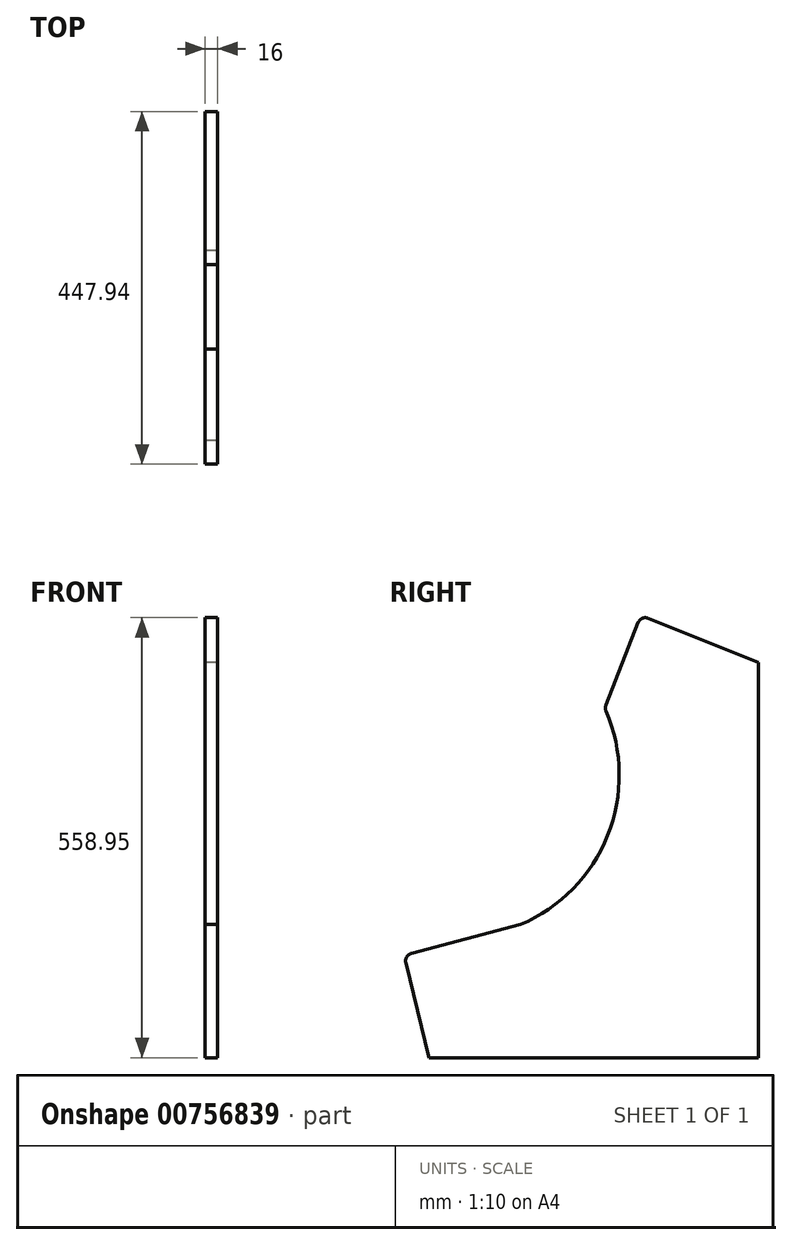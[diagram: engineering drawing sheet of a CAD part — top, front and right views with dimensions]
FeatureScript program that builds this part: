
annotation { "Feature Type Name" : "Feature", "Feature Type Description" : "" }
export const myFeature = defineFeature(function(context is Context, id is Id, definition is map)
    precondition{}
    {
        {
            var Q0;
            Q0=qCreatedBy(makeId("Right.planeOp"),FACE);
            var sketch = newSketch(context, id + "F0", { "sketchPlane" : qUnion([Q0])});
            skLineSegment(sketch, "E0.bottom", {"start": v(209, -251) * mm, "end": v(-209, -251) * mm});
            skLineSegment(sketch, "E0.left", {"start": v(209, -251) * mm, "end": v(209, 251) * mm});
            skPoint(sketch, "E0.middle", {"position": v(0, 0) * mm});
            skLineSegment(sketch, "E1", {"start": v(56.33, 301.57) * mm, "end": v(15.56, 196.86) * mm});
            skLineSegment(sketch, "E2", {"start": v(-93, -82) * mm, "end": v(-231.49, -118.5) * mm});
            skLineSegment(sketch, "E3", {"start": v(-238.65, -130.55) * mm, "end": v(-209, -251) * mm});
            skLineSegment(sketch, "E4", {"start": v(69.38, 307.22) * mm, "end": v(209, 251) * mm});
            skArc(sketch, "E5", {"start": v(-93, -82) * mm, "mid": v(17.56, 31.13) * mm, "end": v(15.7, 189.3) * mm});
            skPoint(sketch, "E6.visualSharp", {"position": v(60, 311) * mm});
            skArc(sketch, "E6.filletArc", {"start": v(69.38, 307.22) * mm, "mid": v(61.68, 307.12) * mm, "end": v(56.33, 301.57) * mm});
            skPoint(sketch, "E7.visualSharp", {"position": v(-241, -121) * mm});
            skArc(sketch, "E7.filletArc", {"start": v(-231.49, -118.5) * mm, "mid": v(-237.54, -123.06) * mm, "end": v(-238.65, -130.55) * mm});
            skPoint(sketch, "E8.visualSharp", {"position": v(14.06, 193) * mm});
            skArc(sketch, "E8.filletArc", {"start": v(15.56, 196.86) * mm, "mid": v(14.88, 193.07) * mm, "end": v(15.7, 189.3) * mm});
            skSolve(sketch);
        }
        {
            var Q0;
            Q0=makeQuery(id+"F0.imprint","IMPRINT",FACE,{"disambiguationData":[TD([[makeQuery(id+"F0.imprint","IMPRINT",EDGE,{"derivedFrom":sQuery(id+"F0.wireOp",EDGE,"E0.bottom")}),-1.0]])]});
            extrude(context, id + "F1", {"entities" : qUnion([Q0]), "depth" : 16 * mm, "offsetDistance" : 25 * mm});
        }
    });
